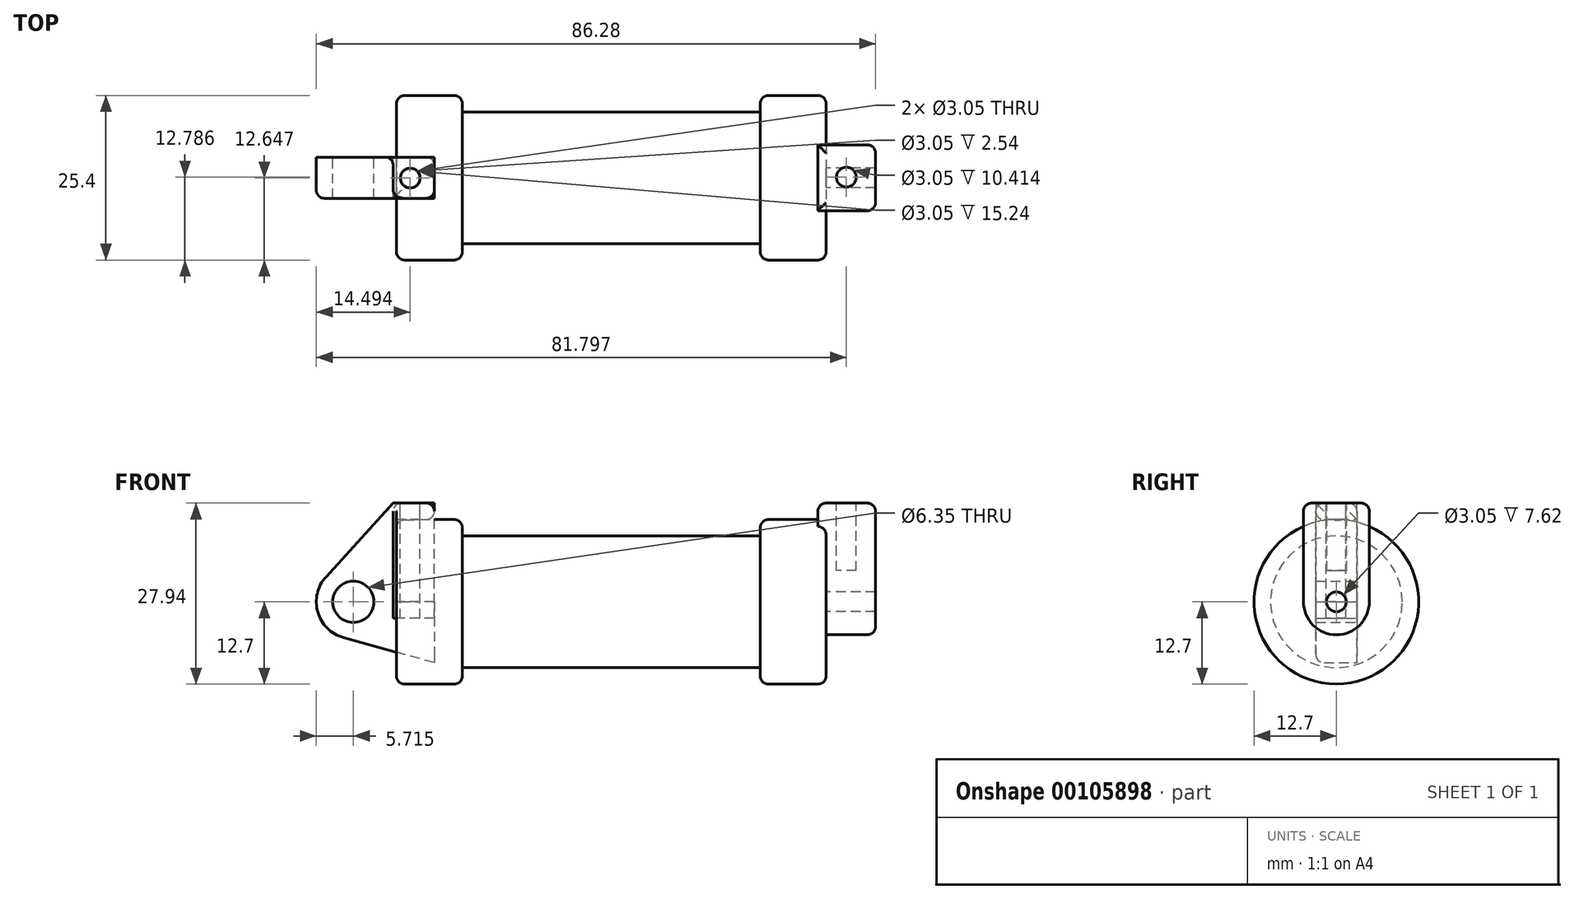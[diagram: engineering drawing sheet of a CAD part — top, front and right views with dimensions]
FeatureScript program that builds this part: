
annotation { "Feature Type Name" : "Feature", "Feature Type Description" : "" }
export const myFeature = defineFeature(function(context is Context, id is Id, definition is map)
    precondition{}
    {
        {
            var Q0;
            Q0=qCreatedBy(makeId("Front.planeOp"),FACE);
            var sketch = newSketch(context, id + "F0", { "sketchPlane" : qUnion([Q0])});
            skLineSegment(sketch, "E0", {"start": v(0, 0) * mm, "end": v(0, 12.7) * mm});
            skLineSegment(sketch, "E1", {"start": v(0, 12.7) * mm, "end": v(10.16, 12.7) * mm});
            skLineSegment(sketch, "E2", {"start": v(10.16, 12.7) * mm, "end": v(10.16, 10.16) * mm});
            skLineSegment(sketch, "E3", {"start": v(10.16, 10.16) * mm, "end": v(56.13, 10.16) * mm});
            skLineSegment(sketch, "E4", {"start": v(56.13, 10.16) * mm, "end": v(56.13, 12.7) * mm});
            skLineSegment(sketch, "E5", {"start": v(56.13, 12.7) * mm, "end": v(66.3, 12.7) * mm});
            skLineSegment(sketch, "E6", {"start": v(66.3, 12.7) * mm, "end": v(66.3, 0) * mm});
            skLineSegment(sketch, "E7", {"start": v(66.3, 0) * mm, "end": v(0, 0) * mm});
            skLineSegment(sketch, "E8", {"start": v(5.84, 15.24) * mm, "end": v(-0.5, 15.24) * mm});
            skLineSegment(sketch, "E9", {"start": v(-0.5, 15.24) * mm, "end": v(-10.88, 3.85) * mm});
            skLineSegment(sketch, "E10", {"start": v(0, 0) * mm, "end": v(-6.65, 0) * mm});
            skCircle(sketch, "E11", {"center": v(-6.65, 0) * mm, "radius": 5.72 * mm});
            skCircle(sketch, "E12", {"center": v(-6.65, 0) * mm, "radius": 3.18 * mm});
            skLineSegment(sketch, "E13", {"start": v(5.84, 15.24) * mm, "end": v(5.84, -9.4) * mm});
            skLineSegment(sketch, "E14", {"start": v(5.84, -9.4) * mm, "end": v(-8.18, -5.5) * mm});
            skSolve(sketch);
        }
        {
            var Q0;
            {var subQ0=sQuery(id+"F0.wireOp",EDGE,"E2");Q0=makeQuery(id+"F0.imprint","IMPRINT",FACE,{"disambiguationData":[TD([[makeQuery(id+"F0.imprint","IMPRINT",EDGE,{"derivedFrom":subQ0}),-1.0]])]});}
            var Q1;
            Q1=sQuery(id+"F0.wireOp",EDGE,"E7");
            revolve(context, id + "F1", {"entities" : qUnion([Q0]), "axis" : qUnion([Q1]), "revolveType" : RevolveType.FULL});
        }
        {
            var Q0;
            {var subQ0=sQuery(id+"F0.wireOp",EDGE,"E0");Q0=makeQuery(id+"F0.imprint","IMPRINT",FACE,{"disambiguationData":[TD([[makeQuery(id+"F0.imprint","IMPRINT",EDGE,{"derivedFrom":subQ0}),-1.0]])]});}
            var Q1;
            Q1=sQuery(id+"F0.wireOp",EDGE,"E7");
            revolve(context, id + "F2", {"operationType" : NewBodyOperationType.ADD, "entities" : qUnion([Q0]), "axis" : qUnion([Q1]), "revolveType" : RevolveType.FULL});
        }
        {
            var Q0;
            {var subQ4=sQuery(id+"F0.wireOp",EDGE,"E12");Q0=makeQuery(id+"F0.imprint","IMPRINT",FACE,{"disambiguationData":[TD([[makeQuery(id+"F0.imprint","IMPRINT",EDGE,{"derivedFrom":subQ4}),-1.0]])]});}
            var Q1;
            {var subQ3=sQuery(id+"F0.wireOp",EDGE,"E0");Q1=makeQuery(id+"F0.imprint","IMPRINT",FACE,{"disambiguationData":[TD([[makeQuery(id+"F0.imprint","IMPRINT",EDGE,{"derivedFrom":subQ3}),1.0]])]});}
            var Q2;
            {var subQ0=sQuery(id+"F0.wireOp",EDGE,"E14");Q2=makeQuery(id+"F0.imprint","IMPRINT",FACE,{"disambiguationData":[TD([[makeQuery(id+"F0.imprint","IMPRINT",EDGE,{"derivedFrom":subQ0}),-1.0]])]});}
            extrude(context, id + "F3", {"entities" : qUnion([Q0, Q1, Q2]), "endBound" : BoundingType.SYMMETRIC, "depth" : 6.35 * mm});
        }
        {
            var Q0;
            Q0=makeQuery(id+"F1.opRevolve","SWEPT_FACE",FACE,{"disambiguationData":[OSD([sQuery(id+"F0.wireOp",EDGE,"E6")])]});
            var sketch = newSketch(context, id + "F4", { "sketchPlane" : qUnion([Q0])});
            skCircle(sketch, "E15", {"center": v(0, 0) * mm, "radius": 1.52 * mm});
            skCircle(sketch, "E16", {"center": v(0, 0) * mm, "radius": 5.08 * mm});
            skLineSegment(sketch, "E17", {"start": v(-5.08, 0) * mm, "end": v(-5.08, 15.24) * mm});
            skLineSegment(sketch, "E18", {"start": v(5.08, 15.24) * mm, "end": v(5.08, 0) * mm});
            skLineSegment(sketch, "E19", {"start": v(-5.08, 15.24) * mm, "end": v(5.08, 15.24) * mm});
            skSolve(sketch);
        }
        {
            var Q0;
            Q0=makeQuery(id+"F4.imprint","IMPRINT",FACE,{"disambiguationData":[TD([[makeQuery(id+"F4.imprint","IMPRINT",EDGE,{"derivedFrom":sQuery(id+"F4.wireOp",EDGE,"E15")}),-1.0]])]});
            var Q1;
            {var subQ0=sQuery(id+"F4.wireOp",EDGE,"E17");var subQ1=sQuery(id+"F4.wireOp",EDGE,"E16");var subQ2=makeQuery(id+"F4.imprint","INTERSECT",VERTEX,{"derivedFrom":[subQ1,subQ0]});Q1=makeQuery(id+"F4.imprint","IMPRINT",FACE,{"disambiguationData":[TD([[makeQuery(id+"F4.imprint","IMPRINT",EDGE,{"disambiguationData":[TD([[subQ2,1.0]])],"derivedFrom":subQ1}),-1.0]])]});}
            var Q2;
            {var subQ0=sQuery(id+"F4.wireOp",EDGE,"E19");Q2=makeQuery(id+"F4.imprint","IMPRINT",FACE,{"disambiguationData":[TD([[makeQuery(id+"F4.imprint","IMPRINT",EDGE,{"derivedFrom":subQ0}),-1.0]])]});}
            extrude(context, id + "F5", {"entities" : qUnion([Q0, Q1, Q2]), "operationType" : NewBodyOperationType.ADD, "depth" : 7.62 * mm});
        }
        {
            var Q0;
            Q0=makeQuery(id+"F5.opExtrude","CAP_FACE",FACE,{"disambiguationData":[OSD([sQuery(id+"F4.wireOp",EDGE,"E15"),sQuery(id+"F4.wireOp",EDGE,"E16"),sQuery(id+"F4.wireOp",EDGE,"E17"),sQuery(id+"F4.wireOp",EDGE,"E18"),sQuery(id+"F4.wireOp",EDGE,"E19")])],"isStart":true});
            extrude(context, id + "F6", {"entities" : qUnion([Q0]), "operationType" : NewBodyOperationType.ADD, "depth" : 1.27 * mm});
        }
        {
            var Q0;
            Q0=makeQuery(id+"F3.opExtrude","SWEPT_FACE",FACE,{"disambiguationData":[OSD([sQuery(id+"F0.wireOp",EDGE,"E8")])]});
            var sketch = newSketch(context, id + "F7", { "sketchPlane" : qUnion([Q0])});
            skCircle(sketch, "E20", {"center": v(2.12, -0.05) * mm, "radius": 1.52 * mm});
            skCircle(sketch, "E21", {"center": v(69.43, 0.09) * mm, "radius": 1.52 * mm});
            skSolve(sketch);
        }
        {
            var Q0;
            Q0=makeQuery(id+"F7.imprint","IMPRINT",FACE,{"disambiguationData":[TD([[makeQuery(id+"F7.imprint","IMPRINT",EDGE,{"derivedFrom":sQuery(id+"F7.wireOp",EDGE,"E20")}),-1.0]])]});
            extrude(context, id + "F8", {"entities" : qUnion([Q0]), "oppositeDirection" : true, "depth" : 17.78 * mm});
        }
        {
            var Q0;
            Q0=makeQuery(id+"F7.imprint","IMPRINT",FACE,{"disambiguationData":[TD([[makeQuery(id+"F7.imprint","IMPRINT",EDGE,{"derivedFrom":sQuery(id+"F7.wireOp",EDGE,"E21")}),1.0]])]});
            extrude(context, id + "F9", {"entities" : qUnion([Q0]), "operationType" : NewBodyOperationType.ADD, "oppositeDirection" : true, "depth" : 10.4 * mm});
        }
        {
            var Q0;
            Q0=makeQuery(id+"F1.opRevolve","SWEPT_EDGE",EDGE,{"disambiguationData":[OSD([sQuery(id+"F0.wireOp",EDGE,"E1"),sQuery(id+"F0.wireOp",EDGE,"E2")])]});
            var Q1;
            Q1=makeQuery(id+"F2.opRevolve","SWEPT_EDGE",EDGE,{"disambiguationData":[OSD([sQuery(id+"F0.wireOp",EDGE,"E0"),sQuery(id+"F0.wireOp",EDGE,"E1")])]});
            var Q2;
            Q2=makeQuery(id+"F1.opRevolve","SWEPT_EDGE",EDGE,{"disambiguationData":[OSD([sQuery(id+"F0.wireOp",EDGE,"E4"),sQuery(id+"F0.wireOp",EDGE,"E5")])]});
            var Q3;
            Q3=makeQuery(id+"F5.boolean.opBoolean","SPLIT",EDGE,{"disambiguationData":[OD(1.0)],"derivedFrom":makeQuery(id+"F1.opRevolve","SWEPT_EDGE",EDGE,{"disambiguationData":[OSD([sQuery(id+"F0.wireOp",EDGE,"E5"),sQuery(id+"F0.wireOp",EDGE,"E6")])]})});
            fillet(context, id + "F10", {"entities" : qUnion([Q0, Q1, Q2, Q3]), "radius" : 1.27 * mm, "tangentPropagation" : true, "allowEdgeOverflow" : false});
        }
        {
            var Q0;
            {var subQ0=sQuery(id+"F0.wireOp",EDGE,"E8");Q0=makeQuery(id+"F8.opExtrude","CAP_EDGE",EDGE,{"disambiguationData":[OSD([subQ0]),TDD([makeQuery(id+"F7.imprint","IMPRINT",EDGE,{"derivedFrom":makeQuery(id+"F3.opExtrude","CAP_EDGE",EDGE,{"disambiguationData":[OSD([subQ0])],"isStart":false})})])],"isStart":true});}
            var Q1;
            Q1=makeQuery(id+"F3.opExtrude","SWEPT_EDGE",EDGE,{"disambiguationData":[OSD([sQuery(id+"F0.wireOp",EDGE,"E8"),sQuery(id+"F0.wireOp",EDGE,"E13")])]});
            var Q2;
            Q2=makeQuery(id+"F3.opExtrude","CAP_EDGE",EDGE,{"disambiguationData":[OSD([sQuery(id+"F0.wireOp",EDGE,"E8")])],"isStart":true});
            var Q3;
            Q3=makeQuery(id+"F8.opExtrude","CAP_EDGE",EDGE,{"disambiguationData":[OSD([sQuery(id+"F0.wireOp",EDGE,"E8"),sQuery(id+"F0.wireOp",EDGE,"E9")])],"isStart":true});
            var Q4;
            Q4=makeQuery(id+"F3.opExtrude","SWEPT_EDGE",EDGE,{"disambiguationData":[OSD([sQuery(id+"F0.wireOp",EDGE,"E1"),sQuery(id+"F0.wireOp",EDGE,"E13")])]});
            var Q5;
            Q5=makeQuery(id+"F3.opExtrude","CAP_EDGE",EDGE,{"disambiguationData":[OSD([sQuery(id+"F0.wireOp",EDGE,"E1")])],"isStart":false});
            var Q6;
            {var subQ0=sQuery(id+"F0.wireOp",EDGE,"E13");Q6=makeQuery(id+"F3.opExtrude","CAP_EDGE",EDGE,{"disambiguationData":[OSD([subQ0]),TDD([makeQuery(id+"F0.imprint","IMPRINT",EDGE,{"disambiguationData":[TD([[makeQuery(id+"F0.imprint","INTERSECT",VERTEX,{"derivedFrom":[sQuery(id+"F0.wireOp",EDGE,"E8"),subQ0]}),-1.0]])],"derivedFrom":subQ0})])],"isStart":true});}
            var Q7;
            {var subQ0=sQuery(id+"F0.wireOp",EDGE,"E13");Q7=makeQuery(id+"F3.opExtrude","CAP_EDGE",EDGE,{"disambiguationData":[OSD([subQ0]),TDD([makeQuery(id+"F0.imprint","IMPRINT",EDGE,{"disambiguationData":[TD([[makeQuery(id+"F0.imprint","INTERSECT",VERTEX,{"derivedFrom":[sQuery(id+"F0.wireOp",EDGE,"E8"),subQ0]}),-1.0]])],"derivedFrom":subQ0})])],"isStart":false});}
            var Q8;
            Q8=makeQuery(id+"F3.opExtrude","CAP_EDGE",EDGE,{"disambiguationData":[OSD([sQuery(id+"F0.wireOp",EDGE,"E9")])],"isStart":false});
            fillet(context, id + "F11", {"entities" : qUnion([Q0, Q1, Q2, Q3, Q4, Q5, Q6, Q7, Q8]), "radius" : 1.27 * mm, "tangentPropagation" : true, "allowEdgeOverflow" : false});
        }
        {
            var Q0;
            {var subQ0=sQuery(id+"F4.wireOp",EDGE,"E19");var subQ1=sQuery(id+"F4.wireOp",EDGE,"E17");Q0=makeQuery(id+"F6.boolean.opBoolean","MERGE",EDGE,{"derivedFrom":[makeQuery(id+"F5.opExtrude","SWEPT_EDGE",EDGE,{"disambiguationData":[OSD([subQ1,subQ0])]}),makeQuery(id+"F6.opExtrude","SWEPT_EDGE",EDGE,{"disambiguationData":[OSD([subQ1,subQ0])]})]});}
            var Q1;
            Q1=makeQuery(id+"F5.opExtrude","CAP_EDGE",EDGE,{"disambiguationData":[OSD([sQuery(id+"F4.wireOp",EDGE,"E19")])],"isStart":false});
            var Q2;
            {var subQ0=sQuery(id+"F4.wireOp",EDGE,"E19");var subQ1=sQuery(id+"F4.wireOp",EDGE,"E18");Q2=makeQuery(id+"F6.boolean.opBoolean","MERGE",EDGE,{"derivedFrom":[makeQuery(id+"F5.opExtrude","SWEPT_EDGE",EDGE,{"disambiguationData":[OSD([subQ1,subQ0])]}),makeQuery(id+"F6.opExtrude","SWEPT_EDGE",EDGE,{"disambiguationData":[OSD([subQ1,subQ0])]})]});}
            var Q3;
            Q3=makeQuery(id+"F6.opExtrude","CAP_EDGE",EDGE,{"disambiguationData":[OSD([sQuery(id+"F4.wireOp",EDGE,"E19")])],"isStart":false});
            var Q4;
            Q4=makeQuery(id+"F5.opExtrude","CAP_EDGE",EDGE,{"disambiguationData":[OSD([sQuery(id+"F4.wireOp",EDGE,"E17")])],"isStart":false});
            var Q5;
            {var subQ0=sQuery(id+"F4.wireOp",EDGE,"E17");var subQ1=sQuery(id+"F4.wireOp",EDGE,"E16");Q5=makeQuery(id+"F5.boolean.opBoolean","SPLIT",EDGE,{"disambiguationData":[TD([makeQuery(id+"F5.opExtrude","SWEPT_FACE",FACE,{"disambiguationData":[OSD([subQ1])]})])],"derivedFrom":makeQuery(id+"F5.opExtrude","CAP_EDGE",EDGE,{"disambiguationData":[OSD([subQ0])],"isStart":true})});}
            fillet(context, id + "F12", {"entities" : qUnion([Q0, Q1, Q2, Q3, Q4, Q5]), "radius" : 1.27 * mm, "tangentPropagation" : true, "allowEdgeOverflow" : false});
        }
        {
            var Q0;
            Q0=makeQuery(id+"F7.imprint","IMPRINT",FACE,{"disambiguationData":[TD([[makeQuery(id+"F7.imprint","IMPRINT",EDGE,{"derivedFrom":sQuery(id+"F7.wireOp",EDGE,"E21")}),1.0]])]});
            extrude(context, id + "F13", {"entities" : qUnion([Q0]), "operationType" : NewBodyOperationType.REMOVE, "oppositeDirection" : true, "depth" : 10.4 * mm});
        }
        {
            var Q0;
            Q0=makeQuery(id+"F7.imprint","IMPRINT",FACE,{"disambiguationData":[TD([[makeQuery(id+"F7.imprint","IMPRINT",EDGE,{"derivedFrom":sQuery(id+"F7.wireOp",EDGE,"E20")}),1.0]])]});
            extrude(context, id + "F14", {"entities" : qUnion([Q0]), "operationType" : NewBodyOperationType.REMOVE, "oppositeDirection" : true, "depth" : 17.78 * mm});
        }
    });
